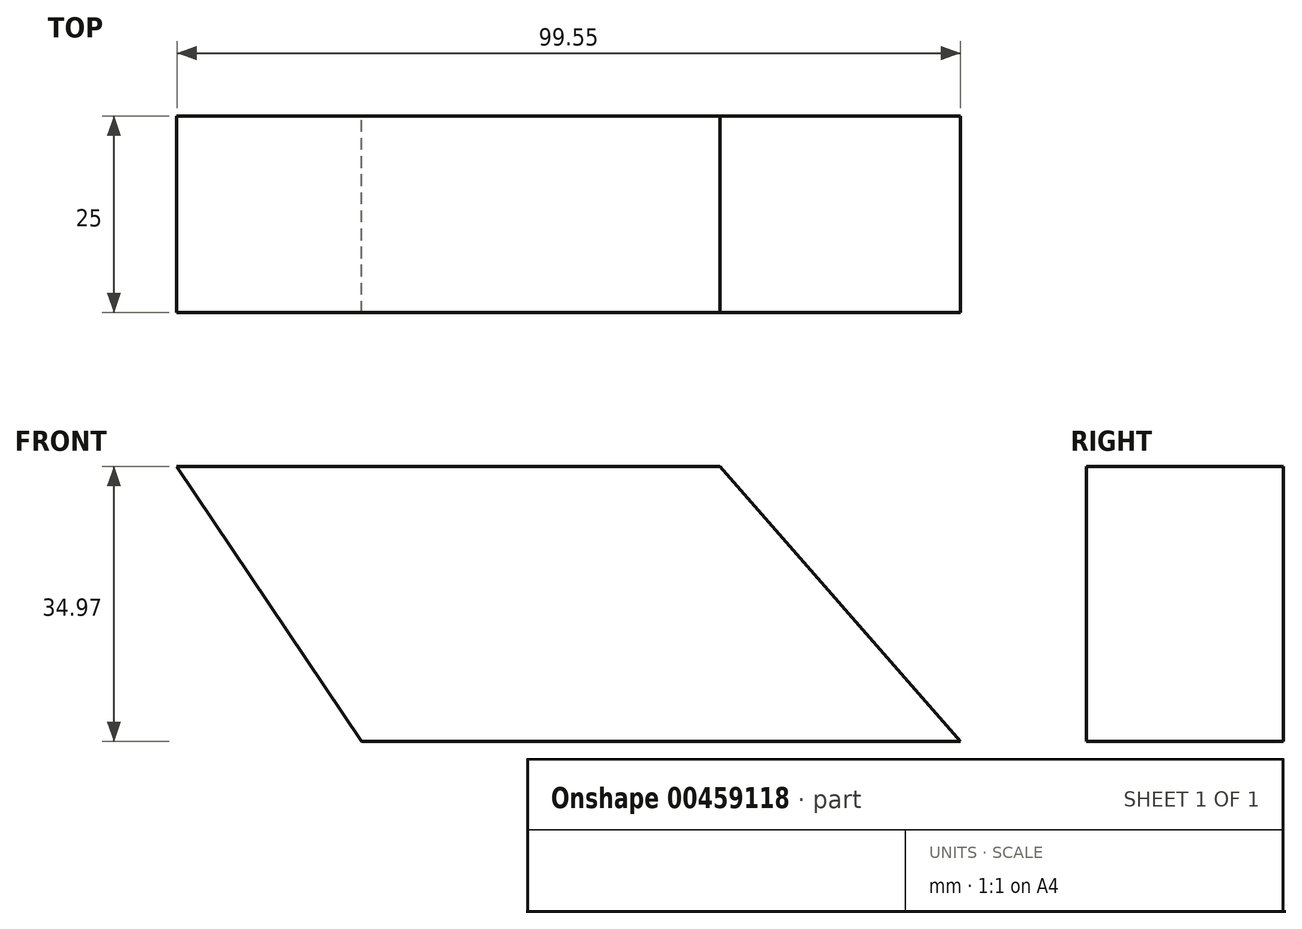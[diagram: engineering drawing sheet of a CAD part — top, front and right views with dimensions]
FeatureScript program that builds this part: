
annotation { "Feature Type Name" : "Feature", "Feature Type Description" : "" }
export const myFeature = defineFeature(function(context is Context, id is Id, definition is map)
    precondition{}
    {
        {
            var Q0;
            Q0=qCreatedBy(makeId("Front.planeOp"),FACE);
            var sketch = newSketch(context, id + "F0", { "sketchPlane" : qUnion([Q0])});
            skLineSegment(sketch, "E0", {"start": v(-50.53, 0) * mm, "end": v(0, 0) * mm});
            skPoint(sketch, "E1.orphan", {"position": v(-72.32, 53.03) * mm});
            skPoint(sketch, "E2.orphan", {"position": v(-72.32, 0) * mm});
            skPoint(sketch, "E3.start.orphan", {"position": v(-72.32, 25.91) * mm});
            skLineSegment(sketch, "E4", {"start": v(-52.29, 0) * mm, "end": v(-50.53, 0) * mm});
            skLineSegment(sketch, "E5", {"start": v(-76.08, 0) * mm, "end": v(-50.53, 0) * mm});
            skLineSegment(sketch, "E6", {"start": v(-30.54, 34.97) * mm, "end": v(-90.54, 34.97) * mm});
            skLineSegment(sketch, "E7", {"start": v(-90.54, 34.97) * mm, "end": v(-30.54, 34.97) * mm});
            skLineSegment(sketch, "E8", {"start": v(-30.54, 34.97) * mm, "end": v(0, 0) * mm});
            skPoint(sketch, "E9.orphan", {"position": v(-78.91, 0) * mm});
            skPoint(sketch, "E10.end.orphan", {"position": v(-63.3, 0) * mm});
            skLineSegment(sketch, "E11", {"start": v(-90.54, 34.97) * mm, "end": v(-99.55, 34.97) * mm});
            skLineSegment(sketch, "E12", {"start": v(-99.55, 34.97) * mm, "end": v(-76.08, 0) * mm});
            skSolve(sketch);
        }
        {
            var Q0;
            Q0 = qSketchRegion(id + "F0", true);
            extrude(context, id + "F1", {"entities" : qUnion([Q0]), "depth" : 25 * mm, "offsetDistance" : 25 * mm});
        }
    });
